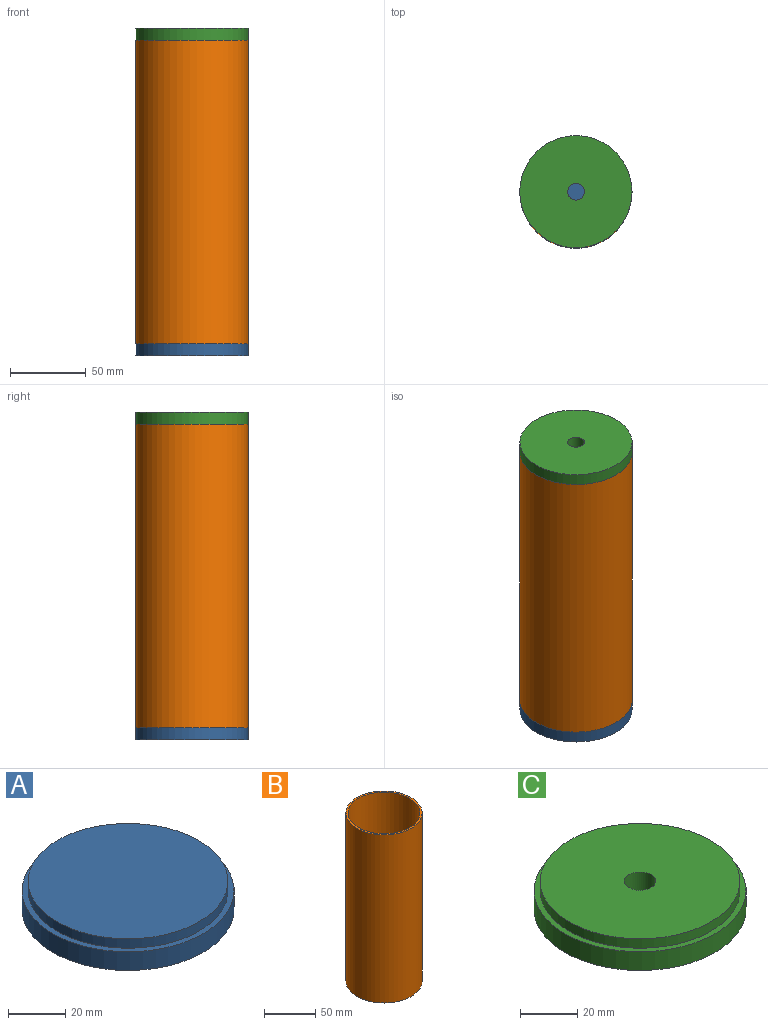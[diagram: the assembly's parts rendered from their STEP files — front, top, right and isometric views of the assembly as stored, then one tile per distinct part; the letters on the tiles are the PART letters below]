
ASSEMBLY  parts=3 mates=2
PART A: 5 faces, bbox 74x74x12 mm
  f0: cylinder r=34.88mm len=69.75mm, axis (0,0,-1), area 876.5mm2, adj f1,f3
  f1: plane 69.75x69.75mm, normal (0,0,1), area 3821mm2, adj f0
  f2: cylinder r=37mm len=74mm, axis (0,0,-1), area 1859.8mm2, adj f3,f4
  f3: plane 74x74mm, normal (0,0,1), area 479.8mm2, adj f0,f2
  f4: plane 74x74mm, normal (0,0,-1), area 4300.8mm2, adj f2
PART B: 4 faces, bbox 74x74x200 mm
  f0: cylinder r=35mm len=200mm, axis (0,0,-1), area 43982.3mm2, adj f2,f3
  f1: cylinder r=37mm len=200mm, axis (0,0,-1), area 46495.6mm2, adj f2,f3
  f2: plane 74x74mm, normal (0,0,1), area 452.4mm2, adj f0,f1
  f3: plane 74x74mm, normal (0,0,-1), area 452.4mm2, adj f0,f1
PART C: 6 faces, bbox 74x74x12 mm
  f0: cylinder r=34.88mm len=69.75mm, axis (0,0,-1), area 876.5mm2, adj f1,f3
  f1: plane 69.75x69.75mm, normal (0,0,1), area 3726mm2, adj f0,f5
  f2: cylinder r=37mm len=74mm, axis (0,0,-1), area 1859.8mm2, adj f3,f4
  f3: plane 74x74mm, normal (0,0,1), area 479.8mm2, adj f0,f2
  f4: plane 74x74mm, normal (0,0,-1), area 4205.8mm2, adj f2,f5
  f5: cylinder r=5.5mm len=12mm, axis (0,0,1), area 414.7mm2, adj f1,f4
PLACE A t=(-96.02,-57.1,50.94)mm
PLACE B t=(-96.02,-57.1,58.94)mm
PLACE C rot(axis=(-1,0,0),180deg) t=(-96.02,-57.1,266.94)mm
MATE fastened B.f1 <-> A.f2  axis (0,0,-1) through (-96.02,-57.1,58.94)mm
MATE fastened C.f2 <-> B.f0  axis (0,0,-1) through (-96.02,-57.1,258.94)mm
